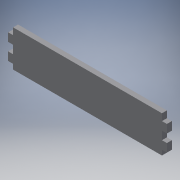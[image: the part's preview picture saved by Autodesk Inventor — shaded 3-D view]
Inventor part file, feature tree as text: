
AUTODESK INVENTOR PART (.ipt)
format: ipt  version: 2019 (Build 230136000, 136)  size: 107,008 bytes
history: native  units: mm
features: reference x8, other x4, extrude x1, sketch x1
ambient origin geometry x8: Origin, YZ Plane, XZ Plane, XY Plane, X Axis, Y Axis, Z Axis, Center Point
bodies: Body1 (feature_tree)
feature tree (14):
  other  "Твердое тело1"
  extrude  "Выдавливание1"  Depth=6.0mm TaperAngle=0.0deg
  sketch  "Эскиз1"
  reference  "Ссылка1"
  reference  "Ссылка2"
  reference  "Ссылка3"
  reference  "Ссылка4"
  reference  "Ссылка5"
  reference  "Ссылка6"
  reference  "Ссылка7"
  reference  "Ссылка8"
  other  "Сборка2"
  other  "боковина:1"
  other  "боковина:2"
